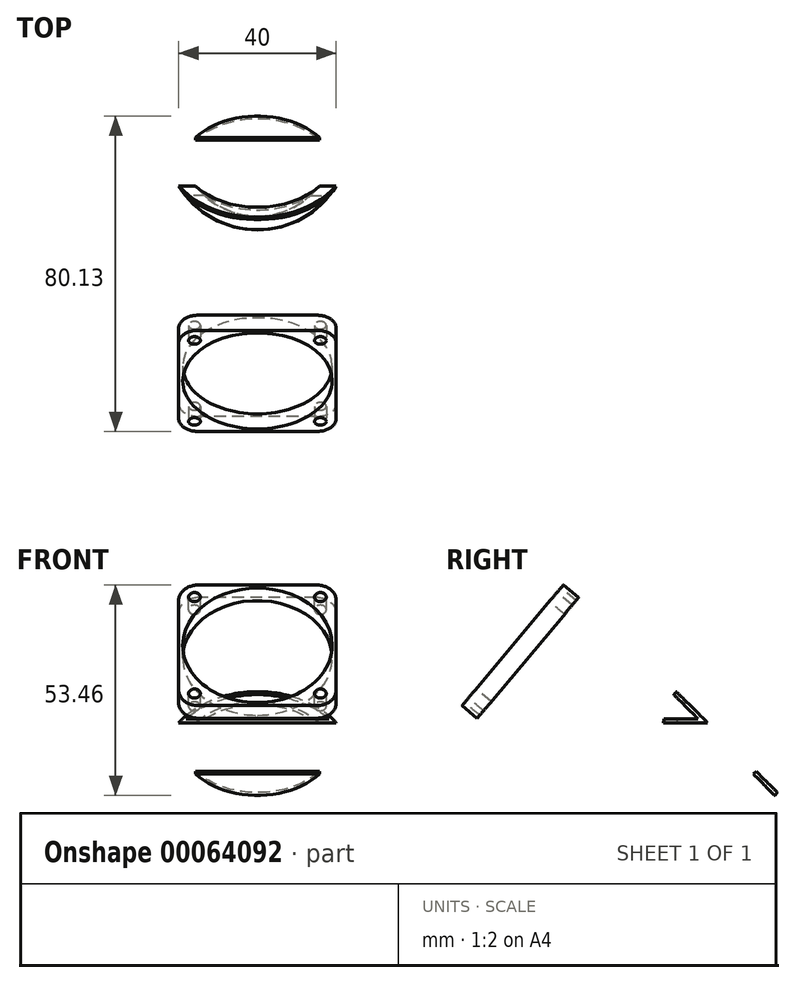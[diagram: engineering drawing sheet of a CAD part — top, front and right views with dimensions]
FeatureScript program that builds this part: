
annotation { "Feature Type Name" : "Feature", "Feature Type Description" : "" }
export const myFeature = defineFeature(function(context is Context, id is Id, definition is map)
    precondition{}
    {
        {
            var Q0;
            Q0=qCreatedBy(makeId("Top.planeOp"),FACE);
            var sketch = newSketch(context, id + "F0", { "sketchPlane" : qUnion([Q0])});
            skCircle(sketch, "E0", {"center": v(0, 0) * mm, "radius": 20 * mm, "construction": true});
            skCircle(sketch, "E1", {"center": v(0, 0) * mm, "radius": 0.2 * mm});
            skSolve(sketch);
        }
        {
            var Q0;
            Q0=qCreatedBy(makeId("Top.planeOp"),FACE);
            var sketch = newSketch(context, id + "F1", { "sketchPlane" : qUnion([Q0])});
            skLineSegment(sketch, "E2", {"start": v(0, 0) * mm, "end": v(0, -45) * mm, "construction": true});
            skLineSegment(sketch, "E3", {"start": v(-15, -45) * mm, "end": v(25, -45) * mm, "construction": true});
            skLineSegment(sketch, "E4.bottom", {"start": v(-20, -41) * mm, "end": v(30, -41) * mm});
            skLineSegment(sketch, "E4.top", {"start": v(-20, -49) * mm, "end": v(30, -49) * mm});
            skLineSegment(sketch, "E4.left", {"start": v(-20, -41) * mm, "end": v(-20, -49) * mm});
            skLineSegment(sketch, "E4.right", {"start": v(30, -41) * mm, "end": v(30, -49) * mm});
            skLineSegment(sketch, "E5", {"start": v(5, -41) * mm, "end": v(5, -49) * mm, "construction": true});
            skPoint(sketch, "E6", {"position": v(5, -45) * mm});
            skCircle(sketch, "E7", {"center": v(-15, -45) * mm, "radius": 1.5 * mm});
            skCircle(sketch, "E8", {"center": v(25, -45) * mm, "radius": 1.5 * mm});
            skLineSegment(sketch, "E9", {"start": v(-20, -41) * mm, "end": v(-20, -23.5) * mm});
            skLineSegment(sketch, "E10", {"start": v(-20, -23.5) * mm, "end": v(30, -23.5) * mm});
            skLineSegment(sketch, "E11", {"start": v(30, -23.5) * mm, "end": v(30, -41) * mm});
            skSolve(sketch);
        }
        {
            var Q0;
            Q0=qCreatedBy(makeId("Top.planeOp"),FACE);
            cPlane(context, id + "F2", {"entities" : qUnion([Q0]), "cplaneType" : CPlaneType.OFFSET, "offset" : 35 * mm, "width" : 150 * mm, "height" : 150 * mm});
        }
        {
            var Q0;
            Q0=qCreatedBy(id+"F2.planeOp",FACE);
            var sketch = newSketch(context, id + "F3", { "sketchPlane" : qUnion([Q0])});
            skCircle(sketch, "E12.0", {"center": v(-15, -45) * mm, "radius": 1.5 * mm});
            skCircle(sketch, "E12.1", {"center": v(25, -45) * mm, "radius": 1.5 * mm});
            skLineSegment(sketch, "E12.2", {"start": v(-20, -41) * mm, "end": v(30, -41) * mm});
            skLineSegment(sketch, "E12.3", {"start": v(-15, -45) * mm, "end": v(25, -45) * mm, "construction": true});
            skLineSegment(sketch, "E12.4", {"start": v(-20, -49) * mm, "end": v(30, -49) * mm});
            skLineSegment(sketch, "E12.5", {"start": v(-20, -41) * mm, "end": v(-20, -49) * mm});
            skLineSegment(sketch, "E12.6", {"start": v(5, -41) * mm, "end": v(5, -49) * mm, "construction": true});
            skLineSegment(sketch, "E12.7", {"start": v(30, -41) * mm, "end": v(30, -49) * mm});
            skSolve(sketch);
        }
        {
            var Q0;
            Q0=qCreatedBy(makeId("Right.planeOp"),FACE);
            var sketch = newSketch(context, id + "F4", { "sketchPlane" : qUnion([Q0])});
            skLineSegment(sketch, "E13", {"start": v(-49, 35) * mm, "end": v(-49, 0) * mm, "construction": true});
            skLineSegment(sketch, "E14", {"start": v(-49, 35) * mm, "end": v(-89, 35) * mm, "construction": true});
            skCircle(sketch, "E15", {"center": v(-49, 35) * mm, "radius": 40 * mm, "construction": true});
            skLineSegment(sketch, "E16", {"start": v(0, 0) * mm, "end": v(-122.29, 0) * mm, "construction": true});
            skSolve(sketch);
        }
        {
            var Q0;
            Q0=qCreatedBy(makeId("Top.planeOp"),FACE);
            var sketch = newSketch(context, id + "F5", { "sketchPlane" : qUnion([Q0])});
            skCircle(sketch, "E17", {"center": v(0, 0) * mm, "radius": 23.5 * mm, "construction": true});
            skCircle(sketch, "E18.0", {"center": v(0, 0) * mm, "radius": 20 * mm, "construction": true});
            skLineSegment(sketch, "E19", {"start": v(0, 0) * mm, "end": v(-23.5, 0) * mm, "construction": true});
            skPoint(sketch, "E20", {"position": v(-20, 0) * mm});
            skLineSegment(sketch, "E21", {"start": v(0, 0) * mm, "end": v(-20, -12.34) * mm, "construction": true});
            skLineSegment(sketch, "E22", {"start": v(0, 0) * mm, "end": v(20, -12.34) * mm, "construction": true});
            skLineSegment(sketch, "E23", {"start": v(20, -12.34) * mm, "end": v(-20, -12.34) * mm, "construction": true});
            skPoint(sketch, "E24", {"position": v(-15.74, -12.34) * mm});
            skPoint(sketch, "E25", {"position": v(15.74, -12.34) * mm});
            skArc(sketch, "E26", {"start": v(-15.74, -12.34) * mm, "mid": v(0, -20) * mm, "end": v(15.74, -12.34) * mm});
            skArc(sketch, "E27", {"start": v(-20, -12.34) * mm, "mid": v(0, -23.5) * mm, "end": v(20, -12.34) * mm});
            skLineSegment(sketch, "E28", {"start": v(-15.74, -12.34) * mm, "end": v(-20, -12.34) * mm});
            skLineSegment(sketch, "E29", {"start": v(15.74, -12.34) * mm, "end": v(20, -12.34) * mm});
            skSolve(sketch);
        }
        {
            var Q0;
            Q0=qCreatedBy(makeId("Right.planeOp"),FACE);
            var sketch = newSketch(context, id + "F6", { "sketchPlane" : qUnion([Q0])});
            skCircle(sketch, "E30", {"center": v(-23.5, 303.06) * mm, "radius": 303.06 * mm, "construction": true});
            skLineSegment(sketch, "E31.0", {"start": v(-49, 35) * mm, "end": v(-89, 35) * mm, "construction": true});
            skLineSegment(sketch, "E31.1", {"start": v(-49, 35) * mm, "end": v(-49, 0) * mm, "construction": true});
            skCircle(sketch, "E32", {"center": v(-49, 35) * mm, "radius": 40 * mm, "construction": true});
            skLineSegment(sketch, "E33", {"start": v(-49, 35) * mm, "end": v(-74.71, 4.36) * mm, "construction": true});
            skLineSegment(sketch, "E34", {"start": v(0, 0) * mm, "end": v(-89, 0) * mm, "construction": true});
            skLineSegment(sketch, "E35", {"start": v(-89, 0) * mm, "end": v(-89, 35) * mm, "construction": true});
            skPoint(sketch, "E36", {"position": v(-23.5, 0) * mm});
            skLineSegment(sketch, "E37", {"start": v(-23.5, 303.06) * mm, "end": v(-23.5, 0) * mm, "construction": true});
            skLineSegment(sketch, "E38", {"start": v(-49, 0) * mm, "end": v(-66.23, 14.46) * mm, "construction": true});
            skSolve(sketch);
        }
        {
            var Q0;
            Q0=sQuery(id+"F6.wireOp",VERTEX,"E38.end");
            var Q1;
            Q1=sQuery(id+"F6.wireOp",EDGE,"E38");
            cPlane(context, id + "F7", {"entities" : qUnion([Q0, Q1]), "cplaneType" : CPlaneType.LINE_POINT, "offset" : 150 * mm, "width" : 150 * mm, "height" : 150 * mm});
        }
        {
            var Q0;
            Q0=qCreatedBy(id+"F7.planeOp",FACE);
            var sketch = newSketch(context, id + "F8", { "sketchPlane" : qUnion([Q0])});
            skLineSegment(sketch, "E39.bottom", {"start": v(20, -4.69) * mm, "end": v(-20, -4.69) * mm});
            skLineSegment(sketch, "E39.top", {"start": v(20, -44.69) * mm, "end": v(-20, -44.69) * mm});
            skLineSegment(sketch, "E39.left", {"start": v(20, -4.69) * mm, "end": v(20, -44.69) * mm});
            skLineSegment(sketch, "E39.right", {"start": v(-20, -4.69) * mm, "end": v(-20, -44.69) * mm});
            skLineSegment(sketch, "E40", {"start": v(0, -4.69) * mm, "end": v(0, -44.69) * mm, "construction": true});
            skCircle(sketch, "E41", {"center": v(0, -24.69) * mm, "radius": 19 * mm});
            skLineSegment(sketch, "E42", {"start": v(20, -4.69) * mm, "end": v(0, -24.69) * mm, "construction": true});
            skLineSegment(sketch, "E43", {"start": v(-20, -24.69) * mm, "end": v(20, -24.69) * mm, "construction": true});
            skCircle(sketch, "E44", {"center": v(16, -8.69) * mm, "radius": 1.5 * mm});
            skCircle(sketch, "E45.MirrorC", {"center": v(-16, -8.69) * mm, "radius": 1.5 * mm});
            skCircle(sketch, "E46.MirrorC", {"center": v(16, -40.69) * mm, "radius": 1.5 * mm});
            skCircle(sketch, "E47.MirrorC", {"center": v(-16, -40.69) * mm, "radius": 1.5 * mm});
            skSolve(sketch);
        }
        {
            var Q0;
            Q0 = qSketchRegion(id + "F8", true);
            extrude(context, id + "F9", {"entities" : qUnion([Q0]), "oppositeDirection" : true, "depth" : 5 * mm});
        }
        {
            var Q0;
            Q0=qCreatedBy(makeId("Top.planeOp"),FACE);
            var sketch = newSketch(context, id + "F10", { "sketchPlane" : qUnion([Q0])});
            skLineSegment(sketch, "E48.0", {"start": v(20, -12.34) * mm, "end": v(-20, -12.34) * mm, "construction": true});
            skArc(sketch, "E48.1", {"start": v(-15.74, -12.34) * mm, "mid": v(0, -20) * mm, "end": v(15.74, -12.34) * mm});
            skArc(sketch, "E48.2", {"start": v(-20, -12.34) * mm, "mid": v(0, -23.5) * mm, "end": v(20, -12.34) * mm});
            skLineSegment(sketch, "E48.3", {"start": v(-15.74, -12.34) * mm, "end": v(-20, -12.34) * mm});
            skLineSegment(sketch, "E48.4", {"start": v(15.74, -12.34) * mm, "end": v(20, -12.34) * mm});
            skSolve(sketch);
        }
        {
            var Q0;
            Q0 = qSketchRegion(id + "F10", true);
            var Q1;
            Q1=sQuery(id+"F5.wireOp",EDGE,"E23");
            revolve(context, id + "F11", {"entities" : qUnion([Q0]), "axis" : qUnion([Q1]), "revolveType" : RevolveType.ONE_DIRECTION, "angle" : 45 * degree});
        }
        {
            var Q0;
            Q0=makeQuery(id+"F11.opRevolve","SWEPT_FACE",FACE,{"disambiguationData":[OSD([sQuery(id+"F10.wireOp",EDGE,"E48.1")])]});
            var Q1;
            Q1=makeQuery(id+"F11.opRevolve","SWEPT_FACE",FACE,{"disambiguationData":[OSD([sQuery(id+"F10.wireOp",EDGE,"E48.2")])]});
            shell(context, id + "F12", {"entities" : qUnion([Q0, Q1]), "thickness" : 1 * mm});
        }
        {
            var Q0;
            Q0=makeQuery(id+"F11.opRevolve","CAP_FACE",FACE,{"disambiguationData":[OSD([sQuery(id+"F10.wireOp",EDGE,"E48.1"),sQuery(id+"F10.wireOp",EDGE,"E48.2"),sQuery(id+"F10.wireOp",EDGE,"E48.3"),sQuery(id+"F10.wireOp",EDGE,"E48.4")])],"isStart":false});
            var sketch = newSketch(context, id + "F13", { "sketchPlane" : qUnion([Q0])});
            skArc(sketch, "E49.0", {"start": v(-15.74, -8.72) * mm, "mid": v(0, -16.39) * mm, "end": v(15.74, -8.72) * mm});
            skLineSegment(sketch, "E50", {"start": v(-15.74, -8.72) * mm, "end": v(15.74, -8.72) * mm});
            skSolve(sketch);
        }
        {
            var Q0;
            Q0 = qSketchRegion(id + "F13", true);
            var Q1;
            {var subQ0=sQuery(id+"F10.wireOp",EDGE,"E48.4");var subQ1=sQuery(id+"F10.wireOp",EDGE,"E48.3");var subQ2=sQuery(id+"F10.wireOp",EDGE,"E48.2");var subQ3=sQuery(id+"F10.wireOp",EDGE,"E48.1");Q1=makeQuery(id+"F12.opShell","OFFSET_FACE",FACE,{"disambiguationData":[OSD([subQ3,subQ2,subQ1,subQ0]),TDD([makeQuery(id+"F11.opRevolve","CAP_FACE",FACE,{"disambiguationData":[OSD([subQ3,subQ2,subQ1,subQ0])],"isStart":false})])]});}
            extrude(context, id + "F14", {"entities" : qUnion([Q0]), "operationType" : NewBodyOperationType.ADD, "endBound" : BoundingType.UP_TO_SURFACE, "oppositeDirection" : true, "endBoundEntityFace" : qUnion([Q1]), "depth" : 1 * mm});
        }
        {
            var Q0;
            Q0=qCreatedBy(makeId("Right.planeOp"),FACE);
            var sketch = newSketch(context, id + "F15", { "sketchPlane" : qUnion([Q0])});
            skLineSegment(sketch, "E51.bottom", {"start": v(-10.24, 0) * mm, "end": v(-14.58, 0) * mm});
            skLineSegment(sketch, "E51.top", {"start": v(-10.24, -1.94) * mm, "end": v(-14.58, -1.94) * mm});
            skLineSegment(sketch, "E51.left", {"start": v(-10.24, 0) * mm, "end": v(-10.24, -1.94) * mm});
            skLineSegment(sketch, "E51.right", {"start": v(-14.58, 0) * mm, "end": v(-14.58, -1.94) * mm});
            skSolve(sketch);
        }
        {
            var Q0;
            Q0 = qSketchRegion(id + "F15", true);
            extrude(context, id + "F16", {"entities" : qUnion([Q0]), "operationType" : NewBodyOperationType.REMOVE, "endBound" : BoundingType.THROUGH_ALL, "oppositeDirection" : true, "depth" : 25 * mm, "hasSecondDirection" : true, "secondDirectionBound" : SecondDirectionBoundingType.THROUGH_ALL, "secondDirectionOppositeDirection" : false, "secondDirectionDepth" : 25 * mm});
        }
        {
            var Q0;
            Q0=makeQuery(id+"F9.opExtrude","CAP_FACE",FACE,{"disambiguationData":[OSD([sQuery(id+"F8.wireOp",EDGE,"E39.bottom"),sQuery(id+"F8.wireOp",EDGE,"E39.top"),sQuery(id+"F8.wireOp",EDGE,"E39.left"),sQuery(id+"F8.wireOp",EDGE,"E39.right"),sQuery(id+"F8.wireOp",EDGE,"E41"),sQuery(id+"F8.wireOp",EDGE,"E44"),sQuery(id+"F8.wireOp",EDGE,"E45.MirrorC"),sQuery(id+"F8.wireOp",EDGE,"E46.MirrorC"),sQuery(id+"F8.wireOp",EDGE,"E47.MirrorC")])],"isStart":true});
            var Q1;
            Q1=makeQuery(id+"F12.opShell","OFFSET_VERTEX",VERTEX,{"disambiguationData":[OSD([sQuery(id+"F10.wireOp",EDGE,"E48.2"),sQuery(id+"F10.wireOp",EDGE,"E48.4")])]});
            cPlane(context, id + "F17", {"entities" : qUnion([Q0, Q1]), "cplaneType" : CPlaneType.PLANE_POINT, "offset" : 150 * mm, "width" : 150 * mm, "height" : 150 * mm});
        }
        {
            var Q0;
            Q0=makeQuery(id+"F9.opExtrude","SWEPT_EDGE",EDGE,{"disambiguationData":[OSD([sQuery(id+"F8.wireOp",EDGE,"E39.bottom"),sQuery(id+"F8.wireOp",EDGE,"E39.left")])]});
            var Q1;
            Q1=makeQuery(id+"F9.opExtrude","SWEPT_EDGE",EDGE,{"disambiguationData":[OSD([sQuery(id+"F8.wireOp",EDGE,"E39.top"),sQuery(id+"F8.wireOp",EDGE,"E39.left")])]});
            var Q2;
            Q2=makeQuery(id+"F9.opExtrude","SWEPT_EDGE",EDGE,{"disambiguationData":[OSD([sQuery(id+"F8.wireOp",EDGE,"E39.bottom"),sQuery(id+"F8.wireOp",EDGE,"E39.right")])]});
            var Q3;
            Q3=makeQuery(id+"F9.opExtrude","SWEPT_EDGE",EDGE,{"disambiguationData":[OSD([sQuery(id+"F8.wireOp",EDGE,"E39.top"),sQuery(id+"F8.wireOp",EDGE,"E39.right")])]});
            fillet(context, id + "F18", {"entities" : qUnion([Q0, Q1, Q2, Q3]), "radius" : 5 * mm, "tangentPropagation" : true, "allowEdgeOverflow" : false});
        }
    });
